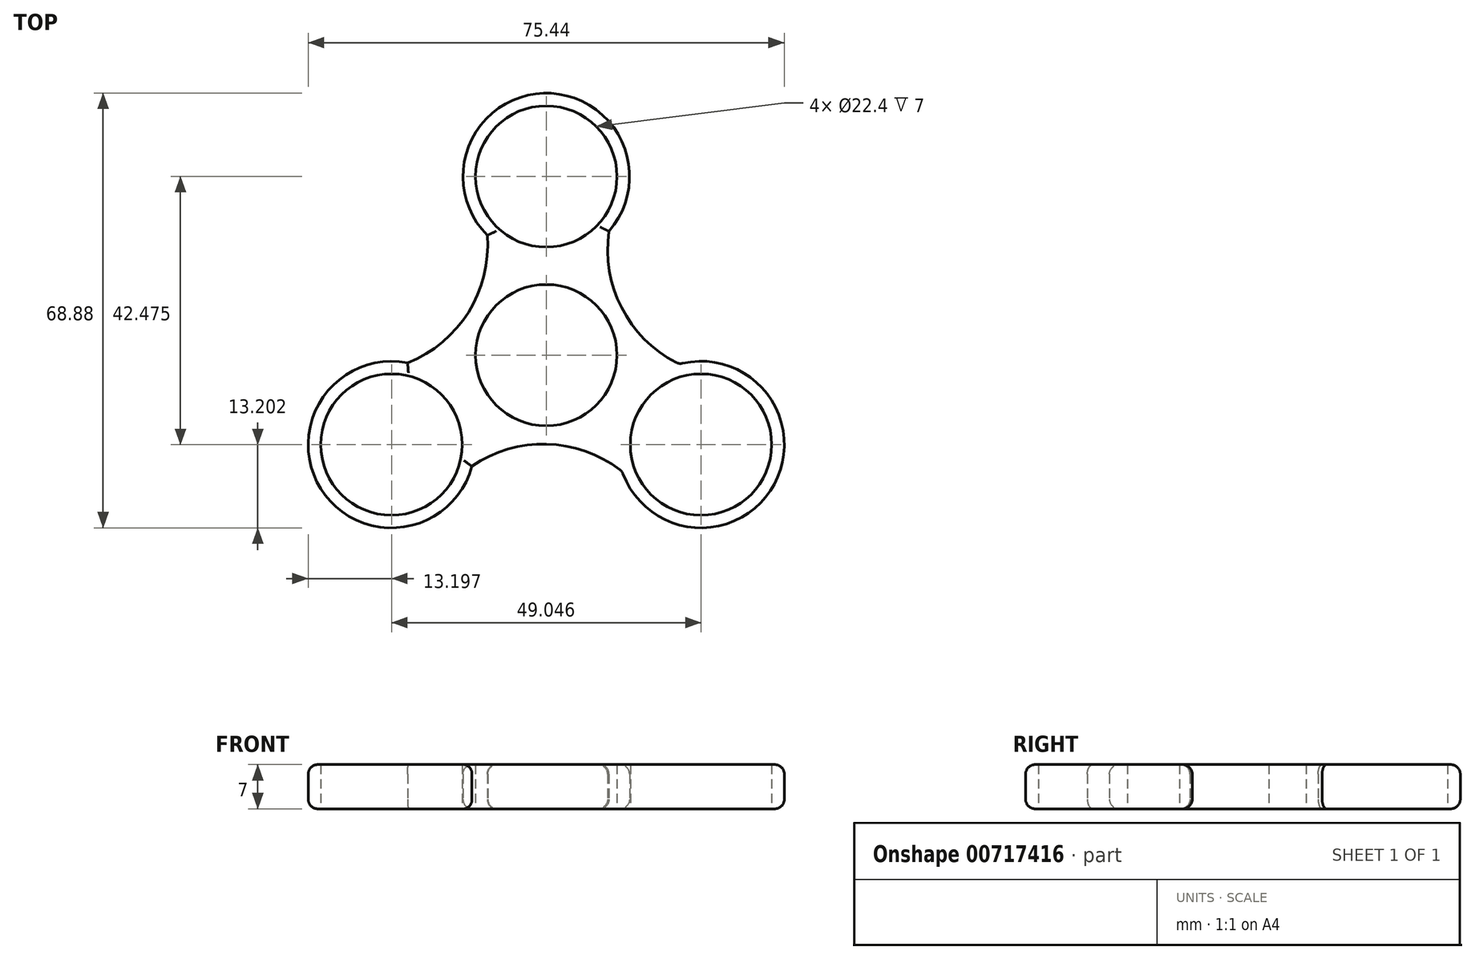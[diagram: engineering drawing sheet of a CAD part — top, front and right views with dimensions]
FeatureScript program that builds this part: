
annotation { "Feature Type Name" : "Feature", "Feature Type Description" : "" }
export const myFeature = defineFeature(function(context is Context, id is Id, definition is map)
    precondition{}
    {
        {
            var Q0;
            Q0=qCreatedBy(makeId("Top.planeOp"),FACE);
            var sketch = newSketch(context, id + "F0", { "sketchPlane" : qUnion([Q0])});
            skCircle(sketch, "E0", {"center": v(0, 0) * mm, "radius": 11.2 * mm});
            skCircle(sketch, "E1", {"center": v(0, 28.32) * mm, "radius": 11.2 * mm});
            skArc(sketch, "E2", {"start": v(9.94, 19.63) * mm, "mid": v(-0.44, 41.5) * mm, "end": v(-9.34, 18.99) * mm});
            skArc(sketch, "E3.1.0", {"start": v(-21.97, -1.2) * mm, "mid": v(-35.73, -21.14) * mm, "end": v(-11.77, -17.58) * mm});
            skCircle(sketch, "E3.1.1", {"center": v(-24.52, -14.16) * mm, "radius": 11.2 * mm});
            skArc(sketch, "E3.2.0", {"start": v(12.03, -18.43) * mm, "mid": v(36.17, -20.37) * mm, "end": v(21.11, -1.4) * mm});
            skCircle(sketch, "E3.2.1", {"center": v(24.52, -14.16) * mm, "radius": 11.2 * mm});
            skArc(sketch, "E4", {"start": v(9.94, 19.63) * mm, "mid": v(12.06, 7.27) * mm, "end": v(21.11, -1.4) * mm});
            skArc(sketch, "E5.1.0", {"start": v(-21.97, -1.2) * mm, "mid": v(-12.33, 6.81) * mm, "end": v(-9.34, 18.99) * mm});
            skArc(sketch, "E5.2.0", {"start": v(12.03, -18.43) * mm, "mid": v(0.27, -14.09) * mm, "end": v(-11.77, -17.58) * mm});
            skSolve(sketch);
        }
        {
            var Q0;
            Q0=makeQuery(id+"F0.imprint","IMPRINT",FACE,{"disambiguationData":[TD([[makeQuery(id+"F0.imprint","IMPRINT",EDGE,{"derivedFrom":sQuery(id+"F0.wireOp",EDGE,"E0")}),-1.0]])]});
            extrude(context, id + "F1", {"entities" : qUnion([Q0]), "depth" : 7 * mm, "offsetDistance" : 25 * mm});
        }
        {
            var Q0;
            Q0=makeQuery(id+"F1.opExtrude","CAP_EDGE",EDGE,{"disambiguationData":[OSD([sQuery(id+"F0.wireOp",EDGE,"E5.2.0")])],"isStart":false});
            var Q1;
            Q1=makeQuery(id+"F1.opExtrude","CAP_EDGE",EDGE,{"disambiguationData":[OSD([sQuery(id+"F0.wireOp",EDGE,"E3.1.0")])],"isStart":false});
            var Q2;
            Q2=makeQuery(id+"F1.opExtrude","CAP_EDGE",EDGE,{"disambiguationData":[OSD([sQuery(id+"F0.wireOp",EDGE,"E5.1.0")])],"isStart":false});
            var Q3;
            Q3=makeQuery(id+"F1.opExtrude","CAP_EDGE",EDGE,{"disambiguationData":[OSD([sQuery(id+"F0.wireOp",EDGE,"E2")])],"isStart":false});
            var Q4;
            Q4=makeQuery(id+"F1.opExtrude","CAP_EDGE",EDGE,{"disambiguationData":[OSD([sQuery(id+"F0.wireOp",EDGE,"E4")])],"isStart":false});
            var Q5;
            Q5=makeQuery(id+"F1.opExtrude","CAP_EDGE",EDGE,{"disambiguationData":[OSD([sQuery(id+"F0.wireOp",EDGE,"E3.2.0")])],"isStart":false});
            var Q6;
            Q6=makeQuery(id+"F1.opExtrude","CAP_EDGE",EDGE,{"disambiguationData":[OSD([sQuery(id+"F0.wireOp",EDGE,"E3.1.0")])],"isStart":true});
            var Q7;
            Q7=makeQuery(id+"F1.opExtrude","CAP_EDGE",EDGE,{"disambiguationData":[OSD([sQuery(id+"F0.wireOp",EDGE,"E5.2.0")])],"isStart":true});
            var Q8;
            Q8=makeQuery(id+"F1.opExtrude","SWEPT_FACE",FACE,{"disambiguationData":[OSD([sQuery(id+"F0.wireOp",EDGE,"E3.2.0")])]});
            var Q9;
            Q9=makeQuery(id+"F1.opExtrude","CAP_EDGE",EDGE,{"disambiguationData":[OSD([sQuery(id+"F0.wireOp",EDGE,"E2")])],"isStart":true});
            var Q10;
            Q10=makeQuery(id+"F1.opExtrude","CAP_EDGE",EDGE,{"disambiguationData":[OSD([sQuery(id+"F0.wireOp",EDGE,"E4")])],"isStart":true});
            var Q11;
            Q11=makeQuery(id+"F1.opExtrude","CAP_EDGE",EDGE,{"disambiguationData":[OSD([sQuery(id+"F0.wireOp",EDGE,"E5.1.0")])],"isStart":true});
            fillet(context, id + "F2", {"entities" : qUnion([Q0, Q1, Q2, Q3, Q4, Q5, Q6, Q7, Q8, Q9, Q10, Q11]), "radius" : 1.5 * mm, "tangentPropagation" : true, "allowEdgeOverflow" : false});
        }
    });
